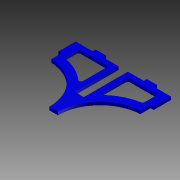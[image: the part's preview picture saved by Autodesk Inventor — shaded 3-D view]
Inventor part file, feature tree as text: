
AUTODESK INVENTOR PART (.ipt)
format: ipt  version: 2012 (Build 160160000, 160)  size: 134,656 bytes
history: native  units: mm
features: extrude x1, sketch x1
ambient origin geometry x8: Origin, YZ Plane, XZ Plane, XY Plane, X Axis, Y Axis, Z Axis, Center Point
feature tree (2):
  extrude  "Extrusion6"  Depth=3.0mm
  sketch  "Sketch1"  dims[d1=46.5mm d3=3.0mm d5=82.5mm d7=45.5mm d10=10.0mm d12=65.0mm d23=3.0mm d24=10.0mm d25=20.0mm d31=8.0mm d32=8.0mm d33=5.0mm d36=15.5mm d37=16.5mm d38=16.75mm d39=5.0mm d40=2.0mm d45=8.0mm d49=68.0mm d50=25.0mm d55=3.0mm d56=0.0mm]
